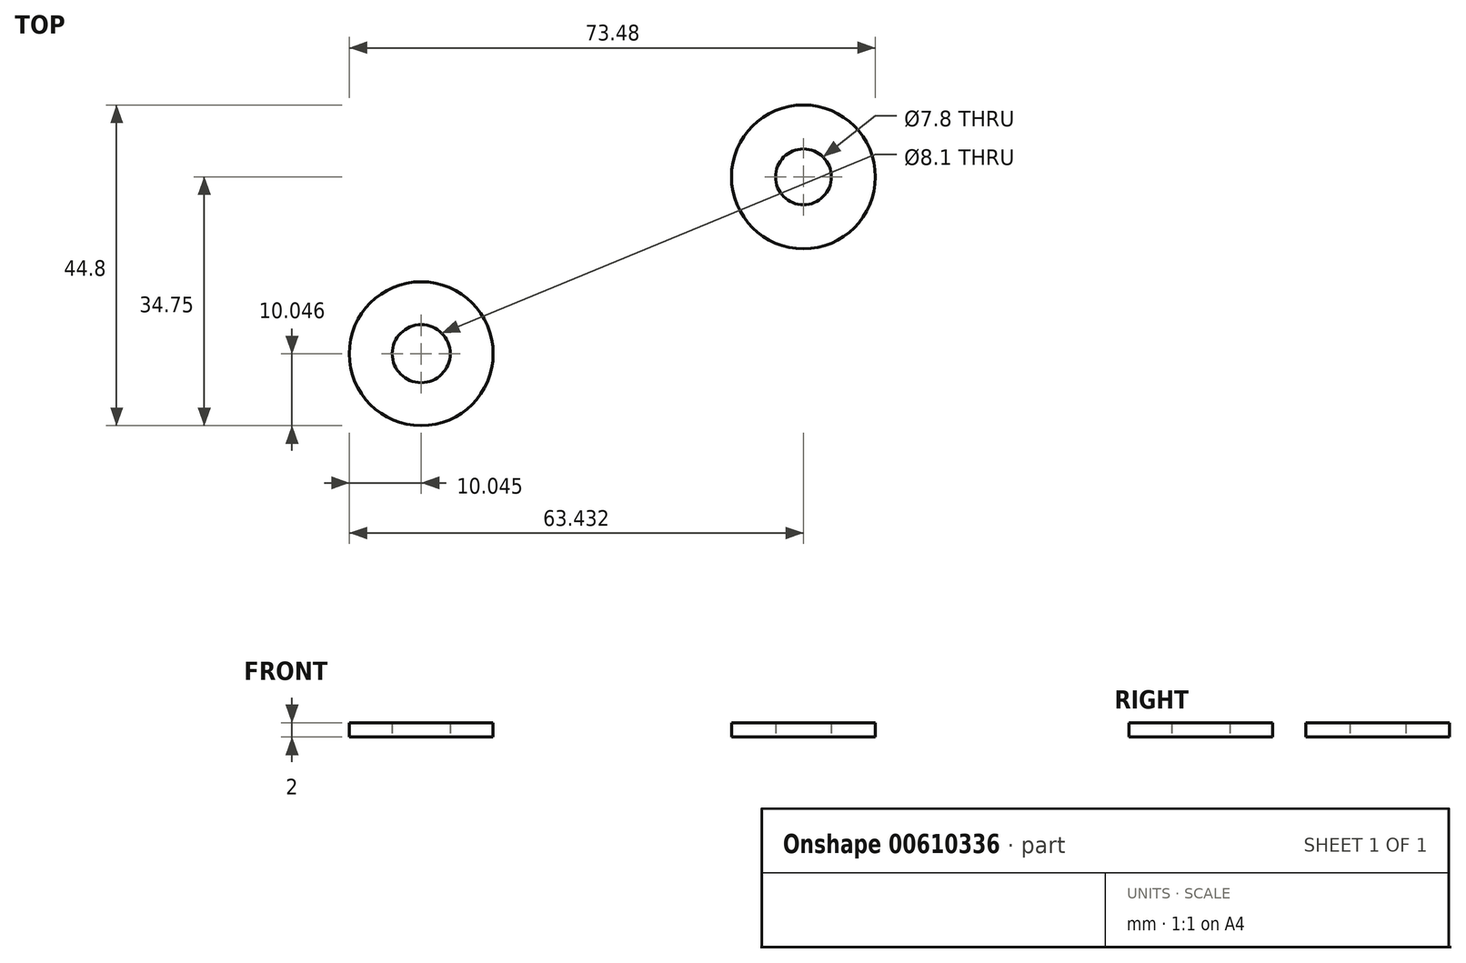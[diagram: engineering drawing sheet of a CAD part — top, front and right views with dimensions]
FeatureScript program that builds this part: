
annotation { "Feature Type Name" : "Feature", "Feature Type Description" : "" }
export const myFeature = defineFeature(function(context is Context, id is Id, definition is map)
    precondition{}
    {
        {
            var Q0;
            Q0=qCreatedBy(makeId("Top.planeOp"),FACE);
            var sketch = newSketch(context, id + "F0", { "sketchPlane" : qUnion([Q0])});
            skCircle(sketch, "E0", {"center": v(-31.97, 19.13) * mm, "radius": 10.05 * mm});
            skCircle(sketch, "E1", {"center": v(-31.97, 19.13) * mm, "radius": 4.05 * mm});
            skCircle(sketch, "E2", {"center": v(21.41, 43.83) * mm, "radius": 10.05 * mm});
            skCircle(sketch, "E3", {"center": v(21.41, 43.83) * mm, "radius": 3.9 * mm});
            skSolve(sketch);
        }
        {
            var Q0;
            Q0 = qSketchRegion(id + "F0", true);
            extrude(context, id + "F1", {"entities" : qUnion([Q0]), "depth" : 2 * mm, "offsetDistance" : 25 * mm});
        }
        {
            var Q0;
            Q0=sQuery(id+"F0.wireOp",EDGE,"E1");
            extrude(context, id + "F2", {"bodyType" : ToolBodyType.SURFACE, "surfaceEntities" : qUnion([Q0]), "depth" : 11 * mm, "offsetDistance" : 25 * mm});
        }
        {
            var Q0;
            Q0=sQuery(id+"F0.wireOp",EDGE,"E0");
            extrude(context, id + "F3", {"bodyType" : ToolBodyType.SURFACE, "surfaceEntities" : qUnion([Q0]), "depth" : .5 * mm, "offsetDistance" : 25 * mm});
        }
        {
            var Q0;
            Q0=sQuery(id+"F0.wireOp",EDGE,"E3");
            extrude(context, id + "F4", {"bodyType" : ToolBodyType.SURFACE, "surfaceEntities" : qUnion([Q0]), "depth" : 11 * mm, "offsetDistance" : 25 * mm});
        }
    });
